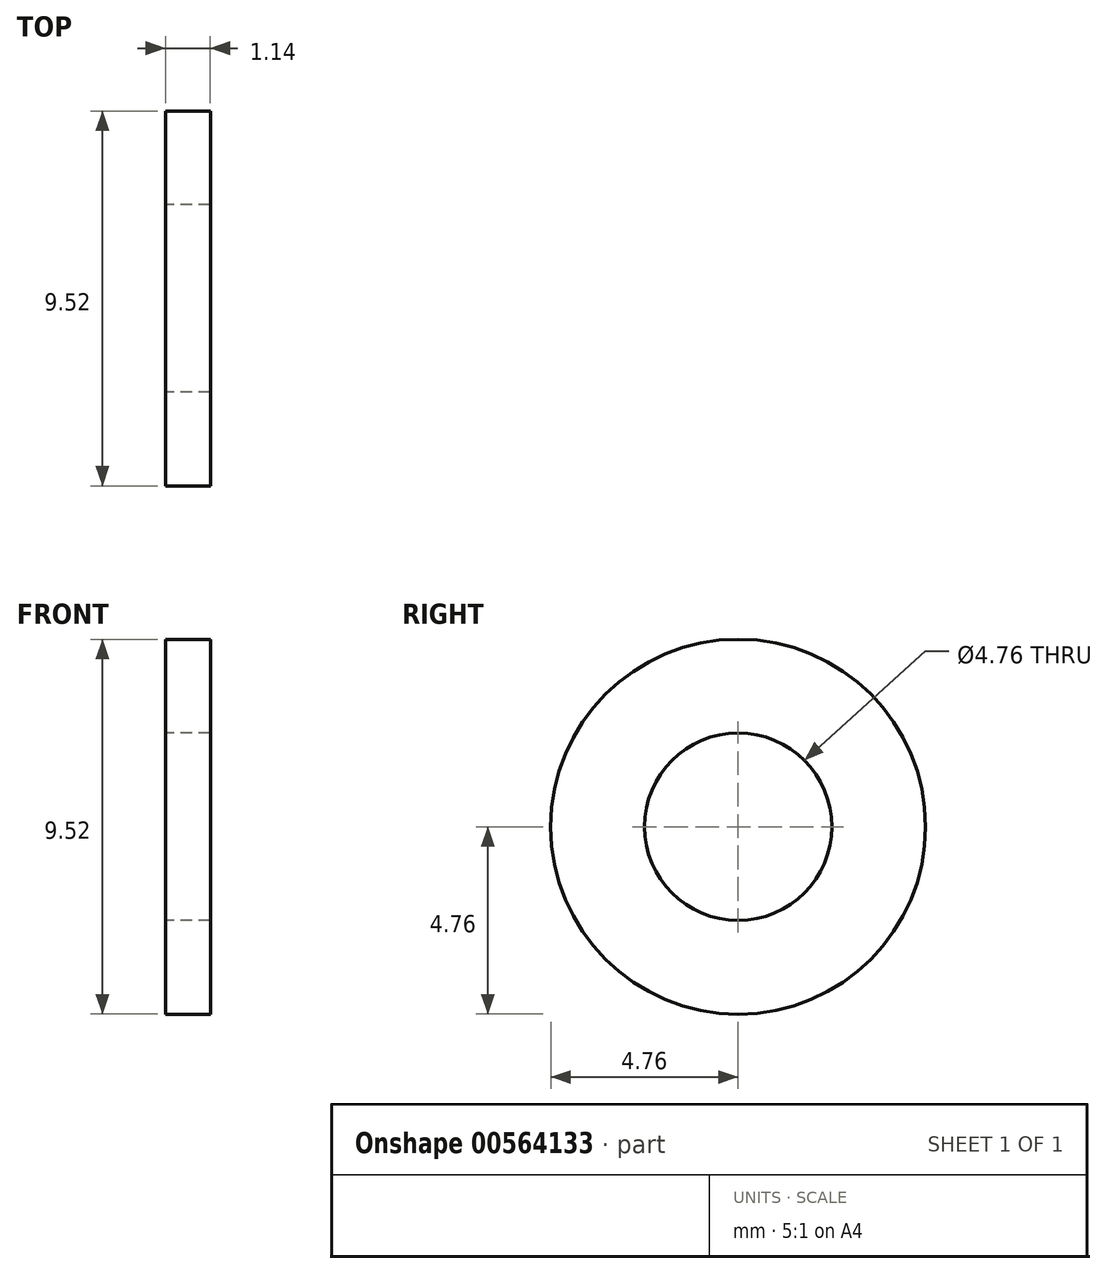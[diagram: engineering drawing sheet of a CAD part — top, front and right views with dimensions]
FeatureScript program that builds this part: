
annotation { "Feature Type Name" : "Feature", "Feature Type Description" : "" }
export const myFeature = defineFeature(function(context is Context, id is Id, definition is map)
    precondition{}
    {
        {
            var Q0;
            Q0=qCreatedBy(makeId("Right.planeOp"),FACE);
            var sketch = newSketch(context, id + "F0", { "sketchPlane" : qUnion([Q0])});
            skCircle(sketch, "E0", {"center": v(0, 0) * mm, "radius": 4.76 * mm});
            skCircle(sketch, "E1", {"center": v(0, 0) * mm, "radius": 2.38 * mm});
            skSolve(sketch);
        }
        {
            var Q0;
            Q0=qSketchRegion(id+"F0",true);
            extrude(context, id + "F1", {"entities" : qUnion([Q0]), "depth" : 1.14 * mm, "offsetDistance" : 25.4 * mm});
        }
    });
